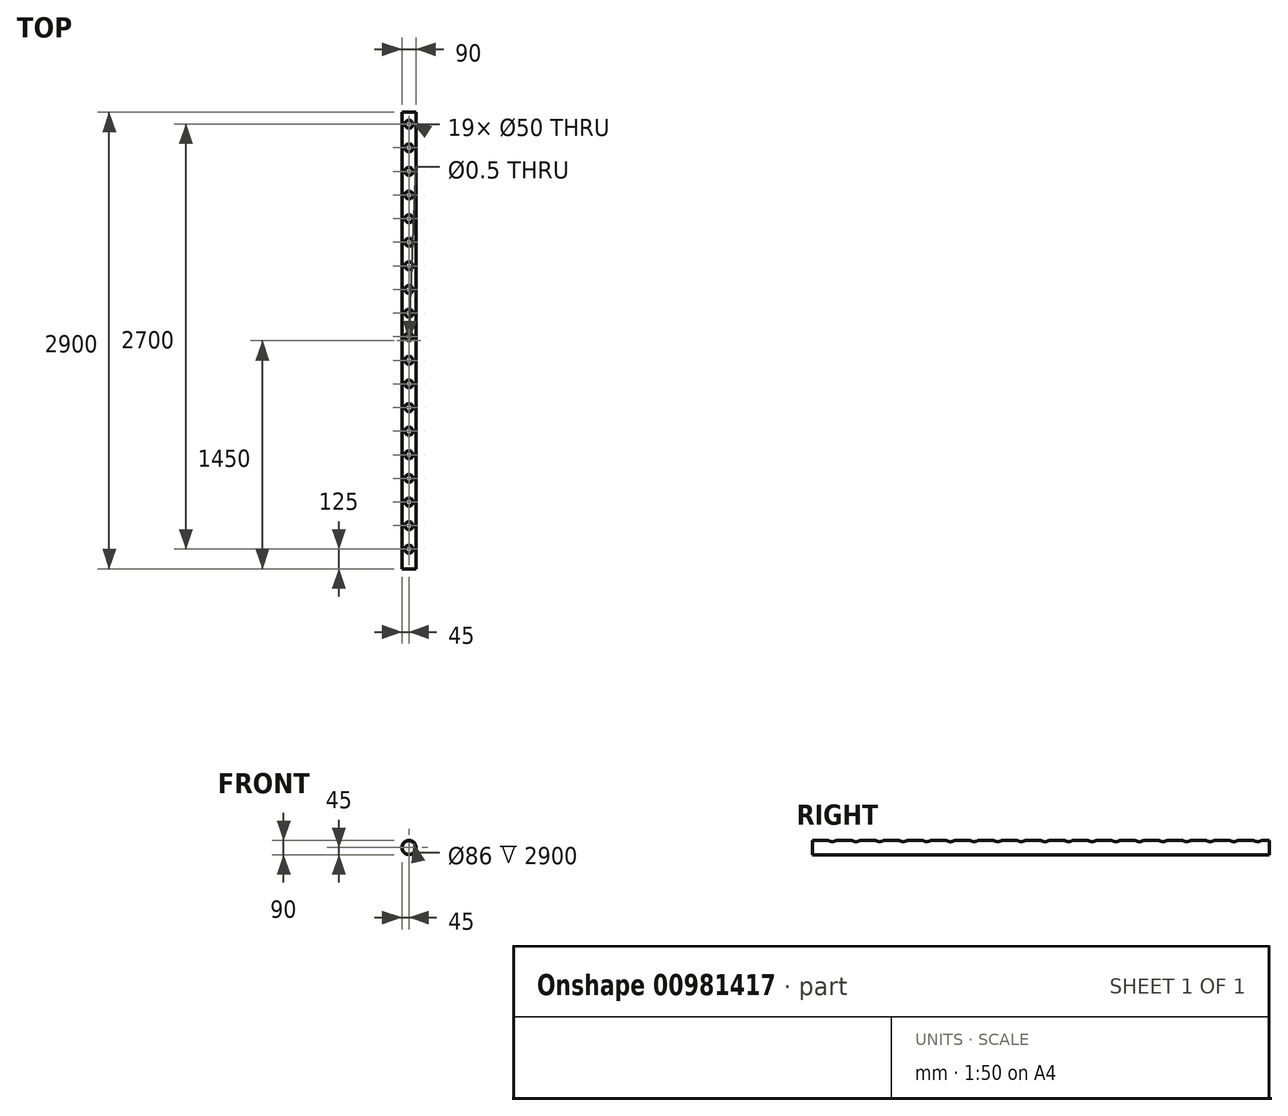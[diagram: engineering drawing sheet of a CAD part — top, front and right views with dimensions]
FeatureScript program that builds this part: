
annotation { "Feature Type Name" : "Feature", "Feature Type Description" : "" }
export const myFeature = defineFeature(function(context is Context, id is Id, definition is map)
    precondition{}
    {
        {
            var Q0;
            Q0=qCreatedBy(makeId("Front.planeOp"),FACE);
            var sketch = newSketch(context, id + "F0", { "sketchPlane" : qUnion([Q0])});
            skCircle(sketch, "E0", {"center": v(0, 0) * mm, "radius": 45 * mm});
            skCircle(sketch, "E1.0", {"center": v(0, 0) * mm, "radius": 43 * mm});
            skSolve(sketch);
        }
        {
            var Q0;
            Q0=qSketchRegion(id+"F0",true);
            extrude(context, id + "F1", {"entities" : qUnion([Q0]), "endBound" : BoundingType.SYMMETRIC, "depth" : 2900 * mm, "offsetDistance" : 25 * mm});
        }
        {
            var Q0;
            Q0=qCreatedBy(makeId("Top.planeOp"),FACE);
            cPlane(context, id + "F2", {"entities" : qUnion([Q0]), "cplaneType" : CPlaneType.OFFSET, "offset" : 45 * mm, "width" : 150 * mm, "height" : 150 * mm});
        }
        {
            var Q0;
            Q0=qCreatedBy(id+"F2.planeOp",FACE);
            var sketch = newSketch(context, id + "F3", { "sketchPlane" : qUnion([Q0])});
            skPoint(sketch, "E2", {"position": v(0, -1325) * mm});
            skPoint(sketch, "E3", {"position": v(0, -1175) * mm});
            skPoint(sketch, "E4", {"position": v(0, -1025) * mm});
            skPoint(sketch, "E5", {"position": v(0, -875) * mm});
            skPoint(sketch, "E6", {"position": v(0, -725) * mm});
            skPoint(sketch, "E7", {"position": v(0, -575) * mm});
            skPoint(sketch, "E8", {"position": v(0, -425) * mm});
            skPoint(sketch, "E9", {"position": v(0, -275) * mm});
            skPoint(sketch, "E10", {"position": v(0, -125) * mm});
            skPoint(sketch, "E11", {"position": v(0, 25) * mm});
            skPoint(sketch, "E12", {"position": v(0, 175) * mm});
            skPoint(sketch, "E13", {"position": v(0, 325) * mm});
            skPoint(sketch, "E14", {"position": v(0, 475) * mm});
            skPoint(sketch, "E15", {"position": v(0, 625) * mm});
            skPoint(sketch, "E16", {"position": v(0, 775) * mm});
            skPoint(sketch, "E17", {"position": v(0, 925) * mm});
            skPoint(sketch, "E18", {"position": v(0, 1075) * mm});
            skPoint(sketch, "E19", {"position": v(0, 1225) * mm});
            skPoint(sketch, "E20", {"position": v(0, 1375) * mm});
            skSolve(sketch);
        }
        {
            var Q0;
            Q0=sQuery(id+"F3.wireOp",VERTEX,"E2");
            var Q1;
            Q1=sQuery(id+"F3.wireOp",VERTEX,"E3");
            var Q2;
            Q2=sQuery(id+"F3.wireOp",VERTEX,"E4");
            var Q3;
            Q3=sQuery(id+"F3.wireOp",VERTEX,"E5");
            var Q4;
            Q4=sQuery(id+"F3.wireOp",VERTEX,"E6");
            var Q5;
            Q5=sQuery(id+"F3.wireOp",VERTEX,"E7");
            var Q6;
            Q6=sQuery(id+"F3.wireOp",VERTEX,"E8");
            var Q7;
            Q7=sQuery(id+"F3.wireOp",VERTEX,"E9");
            var Q8;
            Q8=sQuery(id+"F3.wireOp",VERTEX,"E10");
            var Q9;
            Q9=sQuery(id+"F3.wireOp",VERTEX,"E11");
            var Q10;
            Q10=sQuery(id+"F3.wireOp",VERTEX,"E12");
            var Q11;
            Q11=sQuery(id+"F3.wireOp",VERTEX,"E13");
            var Q12;
            Q12=sQuery(id+"F3.wireOp",VERTEX,"E14");
            var Q13;
            Q13=sQuery(id+"F3.wireOp",VERTEX,"E15");
            var Q14;
            Q14=sQuery(id+"F3.wireOp",VERTEX,"E16");
            var Q15;
            Q15=sQuery(id+"F3.wireOp",VERTEX,"E17");
            var Q16;
            Q16=sQuery(id+"F3.wireOp",VERTEX,"E18");
            var Q17;
            Q17=sQuery(id+"F3.wireOp",VERTEX,"E19");
            var Q18;
            Q18=sQuery(id+"F3.wireOp",VERTEX,"E20");
            var Q19;
            Q19=sQuery(id+"F3.wireOp",VERTEX,"4217ffee-23aa-4e57-b56b-1031955cdd20");
            var Q20;
            Q20=sQuery(id+"F3.wireOp",VERTEX,"f9e667d2-43f0-46cb-85dd-7700daad2ab1");
            var Q21;
            Q21=sQuery(id+"F3.wireOp",VERTEX,"a141cc4f-d6fa-4136-a428-d91cc8b08e23");
            var Q22;
            Q22=sQuery(id+"F3.wireOp",VERTEX,"6950c5e6-caf7-4953-8c5b-56709a9cffe9");
            var Q23;
            Q23=sQuery(id+"F3.wireOp",VERTEX,"1581daf2-9304-4365-a3cc-e960652a3bf4");
            var Q24;
            Q24=sQuery(id+"F3.wireOp",VERTEX,"25a0b738-50ad-46bb-ba52-db4eb22869ea");
            var Q25;
            Q25=sQuery(id+"F3.wireOp",VERTEX,"23c6b068-1da5-4682-a93c-07f6e733a235");
            var Q26;
            Q26=sQuery(id+"F3.wireOp",VERTEX,"77491461-51bd-4097-a69a-b50156a0fef7");
            var Q27;
            Q27=sQuery(id+"F3.wireOp",VERTEX,"89e2eaf9-af87-4198-a739-5b01357332c3");
            var Q28;
            Q28=sQuery(id+"F3.wireOp",VERTEX,"a31ac070-19d1-4092-b391-6f630edb761b");
            var Q29;
            Q29=makeQuery(id+"F1.opExtrude","SWEPT_BODY",BODY,{"disambiguationData":[OSD([sQuery(id+"F0.wireOp",EDGE,"E0"),sQuery(id+"F0.wireOp",EDGE,"E1.0")])]});
            hole(context, id + "F4", {"style" : HoleStyle.SIMPLE, "endStyle" : HoleEndStyle.BLIND, "holeDiameter" : 50 * mm, "majorDiameter" : 5 * mm, "holeDepth" : 50 * mm, "isTappedThrough" : true, "tappedDepth" : 12 * mm, "tapClearance" : 3, "startFromSketch" : true, "locations" : qUnion([Q0, Q1, Q2, Q3, Q4, Q5, Q6, Q7, Q8, Q9, Q10, Q11, Q12, Q13, Q14, Q15, Q16, Q17, Q18, Q19, Q20, Q21, Q22, Q23, Q24, Q25, Q26, Q27, Q28]), "scope" : qUnion([Q29])});
        }
        {
            var Q0;
            Q0=qCreatedBy(makeId("Top.planeOp"),FACE);
            var sketch = newSketch(context, id + "F5", { "sketchPlane" : qUnion([Q0])});
            skPoint(sketch, "E21", {"position": v(0, 0) * mm});
            skSolve(sketch);
        }
        {
            var Q0;
            Q0=sQuery(id+"F5.wireOp",VERTEX,"E21");
            var Q1;
            Q1=makeQuery(id+"F1.opExtrude","SWEPT_BODY",BODY,{"disambiguationData":[OSD([sQuery(id+"F0.wireOp",EDGE,"E0"),sQuery(id+"F0.wireOp",EDGE,"E1.0")])]});
            hole(context, id + "F6", {"style" : HoleStyle.SIMPLE, "endStyle" : HoleEndStyle.BLIND, "holeDiameter" : 0.5 * mm, "majorDiameter" : 5 * mm, "holeDepth" : 50 * mm, "isTappedThrough" : true, "tappedDepth" : 12 * mm, "tapClearance" : 3, "startFromSketch" : true, "locations" : qUnion([Q0]), "scope" : qUnion([Q1])});
        }
    });
